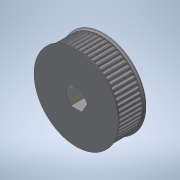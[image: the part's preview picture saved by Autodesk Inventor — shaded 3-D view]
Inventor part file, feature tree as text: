
AUTODESK INVENTOR PART (.ipt)
format: ipt  version: 2022.3 (Build 263350000, 350)  size: 509,440 bytes
history: native  units: in
note: dims shown in document units (in); Inventor stores cm internally (conversion verified against a paired STEP export)
features: extrude x7, sketch x7, fillet x2, pattern_circular x2, mirror x2, chamfer x2, other x1
ambient origin geometry x8: Origin, YZ Plane, XZ Plane, XY Plane, X Axis, Y Axis, Z Axis, Center Point
bodies: Solid1 (feature_tree)
feature tree (23):
  other  "Hex Bore"
  extrude  "HTD Base"  Depth=0.6299in TaperAngle=0.0deg
  extrude  "HTD Base Tooth"  Depth=0.0113in
  fillet  "HTD Base Tooth pt. 2"  [1 undecoded]
  pattern_circular  "HTD Teeth"  Count=60  [1 undecoded]
  extrude  "HTD Flange"  Depth=0.0394in
  mirror  "HTD Flanges"
  chamfer  "HTD Flange Chamfer"  Distance=0.0787in Angle=45.0deg
  extrude  "GT2 Base"  Depth=0.52in
  extrude  "GT2 Base Tooth"  TaperAngle=0.0deg  [1 undecoded]
  fillet  "GT2 Base Tooth pt. 2"  Radius=0.52in
  pattern_circular  "GT2 Teeth"  [2 undecoded]
  extrude  "GT2 Flange"  Depth=0.0591in
  mirror  "GT2 Flanges"
  chamfer  "GT2 Flange Chamfer"  Distance=0.6299in
  extrude  "Circle Bore"  TaperAngle=0.0deg  [1 undecoded]
  sketch  "Sketch1"  dims[d0=3.7146in d1=0.6299in d2=0.0in]
  sketch  "Sketch2"  dims[d3=0.1208in d5=0.0113in d6=0.0in d7=0.0in]
  sketch  "Sketch3"  dims[d8=0.0169in d9=23.622in]
  sketch  "Sketch4"  dims[d10=360.0deg d12=0.0394in]
  sketch  "Sketch5"  dims[d13=0.0591in]
  sketch  "Sketch6"  dims[d14=0.0in]
  sketch  "Sketch7"  dims[d15=0.0394in d16=0.0787in d17=45.0deg d18=0.52in d19=0.0in d20=0.0in d21=0.52in d22=0.0in d23=0.0in d24=2.2257in d25=0.6299in d26=0.0in d27=0.0727in d28=0.0075in d29=0.0in d30=0.0in d31=0.0118in d32=23.622in d33=360.0deg d35=0.0394in d36=0.0591in d37=0.0in d38=0.0394in d39=0.0787in d40=45.0deg]
note: 6 required parameter values undecoded (feature->parameter linkage not recoverable at this tier; creation-order binding heuristic only, values carry confidence <= 0.55)
